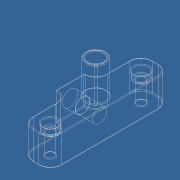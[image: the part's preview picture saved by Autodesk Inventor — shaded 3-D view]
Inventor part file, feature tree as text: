
AUTODESK INVENTOR PART (.ipt)
format: ipt  version: 2018.2 (Build 222227000, 227)  size: 267,776 bytes
history: native  units: in
note: dims shown in document units (in); Inventor stores cm internally (conversion verified against a paired STEP export)
features: sketch x6, hole x3, extrude x2, fillet x2, revolve x1
ambient origin geometry x8: Origin, YZ Plane, XZ Plane, XY Plane, X Axis, Y Axis, Z Axis, Center Point
bodies: Solid1 (feature_tree)
feature tree (14):
  revolve  "Revolution1"  [1 undecoded]
  hole  "Hole4"  [1 undecoded]
  extrude  "Extrusion1"  Depth=0.75in
  hole  "Hole3"  [1 undecoded]
  extrude  "Extrusion2"  Depth=0.625in
  hole  "Hole5"  [1 undecoded]
  fillet  "Fillet1"  Radius=0.016in
  fillet  "Fillet2"  Radius=0.625in
  sketch  "Sketch1"  dims[d0=0.3563in d1=0.0394in]
  sketch  "Sketch3"  dims[d2=0.4331in d3=0.625in]
  sketch  "Sketch4"  dims[d4=0.625in d5=0.75in]
  sketch  "Sketch5"  dims[d6=90.0deg d23=2.625in]
  sketch  "Sketch7"  dims[d24=0.625in d25=0.0in d26=2.0in]
  sketch  "Sketch8"  dims[d27=0.177in d28=0.273in d29=0.313in d30=0.164in d31=0.5635in d32=0.6in d33=0.8108in d34=0.25in d35=0.016in d36=0.05in d37=0.75in d38=0.375in d39=0.25in d40=0.5635in d41=1.0625in d42=0.8108in d43=0.625in d44=0.25in d45=0.0in d46=0.313in d47=0.273in d48=0.0246in d49=0.327in d50=0.375in d51=0.25in d52=0.5635in d53=0.65in d54=0.0in]
note: 4 required parameter values undecoded (feature->parameter linkage not recoverable at this tier; creation-order binding heuristic only, values carry confidence <= 0.55)